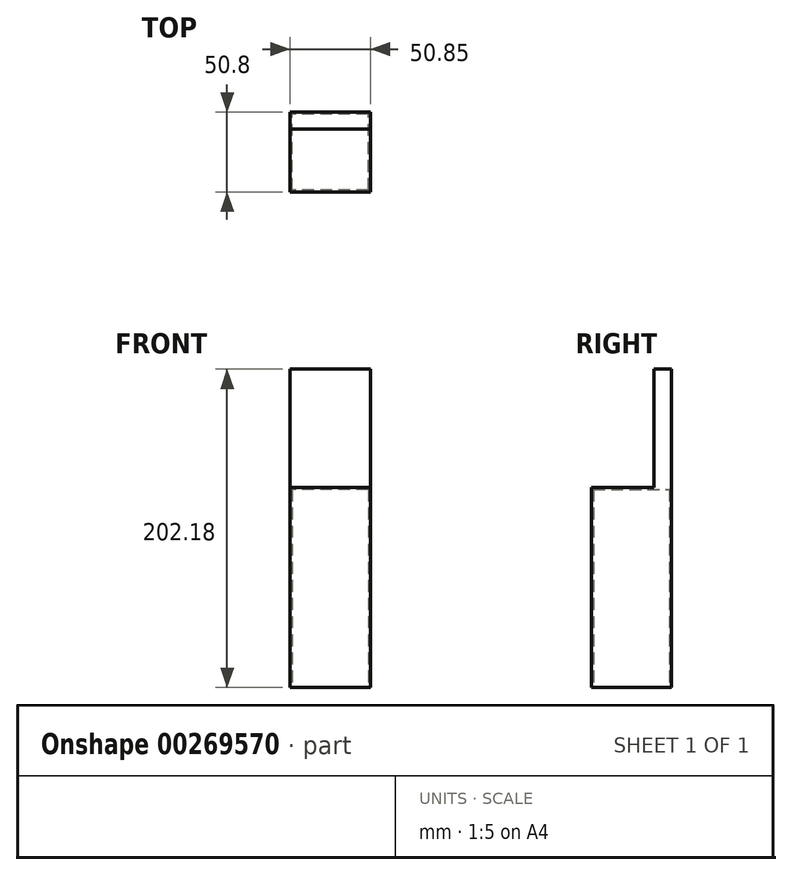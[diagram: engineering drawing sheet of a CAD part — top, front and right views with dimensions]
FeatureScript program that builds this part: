
annotation { "Feature Type Name" : "Feature", "Feature Type Description" : "" }
export const myFeature = defineFeature(function(context is Context, id is Id, definition is map)
    precondition{}
    {
        {
            var Q0;
            Q0=qCreatedBy(makeId("Right.planeOp"),FACE);
            var sketch = newSketch(context, id + "F0", { "sketchPlane" : qUnion([Q0])});
            skLineSegment(sketch, "E0.bottom", {"start": v(-48, 64.06) * mm, "end": v(2.8, 64.06) * mm});
            skLineSegment(sketch, "E0.top", {"start": v(-48, -62.94) * mm, "end": v(2.8, -62.94) * mm});
            skLineSegment(sketch, "E0.left", {"start": v(-48, 64.06) * mm, "end": v(-48, -62.94) * mm});
            skLineSegment(sketch, "E0.right", {"start": v(2.8, 64.06) * mm, "end": v(2.8, -62.94) * mm});
            skSolve(sketch);
        }
        {
            var Q0;
            Q0 = qSketchRegion(id + "F0", true);
            extrude(context, id + "F1", {"entities" : qUnion([Q0]), "depth" : 50.85 * mm});
        }
        {
            var Q0;
            Q0=makeQuery(id+"F1.opExtrude","SWEPT_FACE",FACE,{"disambiguationData":[OSD([sQuery(id+"F0.wireOp",EDGE,"E0.top")])]});
            shell(context, id + "F2", {"entities" : qUnion([Q0]), "thickness" : 1.27 * mm});
        }
        {
            var Q0;
            Q0=makeQuery(id+"F1.opExtrude","SWEPT_FACE",FACE,{"disambiguationData":[OSD([sQuery(id+"F0.wireOp",EDGE,"E0.bottom")])]});
            var sketch = newSketch(context, id + "F3", { "sketchPlane" : qUnion([Q0])});
            skLineSegment(sketch, "E1.bottom", {"start": v(50.85, 2.8) * mm, "end": v(0, 2.8) * mm});
            skLineSegment(sketch, "E1.top", {"start": v(50.85, -8.1) * mm, "end": v(0, -8.1) * mm});
            skLineSegment(sketch, "E1.left", {"start": v(50.85, 2.8) * mm, "end": v(50.85, -8.1) * mm});
            skLineSegment(sketch, "E1.right", {"start": v(0, 2.8) * mm, "end": v(0, -8.1) * mm});
            skSolve(sketch);
        }
        {
            var Q0;
            Q0=makeQuery(id+"F3.imprint","IMPRINT",FACE,{"disambiguationData":[TD([[makeQuery(id+"F3.imprint","IMPRINT",EDGE,{"derivedFrom":sQuery(id+"F3.wireOp",EDGE,"E1.bottom")}),1.0]])]});
            extrude(context, id + "F4", {"entities" : qUnion([Q0]), "operationType" : NewBodyOperationType.ADD, "depth" : 75.18 * mm});
        }
    });
